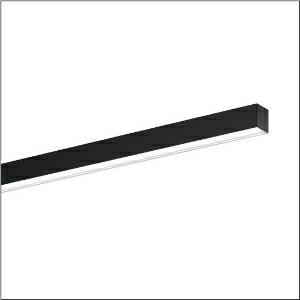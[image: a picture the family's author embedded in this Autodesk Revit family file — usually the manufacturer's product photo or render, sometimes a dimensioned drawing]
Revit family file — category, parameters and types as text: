
# Revit family: silica_21_51mx23tat4b
name_source: partatom
category: Lighting Fixtures
units: mm (PartAtom-declared; Revit-internal decimal feet)

## family parameters
Cut with Voids When Loaded = No
Host = Face
Light Source = No
Part Type = Normal
Room Calculation Point = No
Round Connector Dimension = Use Diameter
Shared = No

## types (1)
- --- (1 x LED, 3230 lm, 32.4 W, 6500K)
    Apparent Load = 32 VA
    CIE Flux Codes = 78 96 99 100 100
    Color Rendering = 80
    Color Temperature = 6500K
    Default Elevation = 1800 mm
    Description = Silica 21, office luminaire, primary optical cover: prismatic diffuser, of PMMA, CAT 2 (L<= 3000cd/m²), light emission: direct distribution, primary light characteristic: symmetric, installation type: surface-mounted, LED, rated luminous flux: 3.230lm, luminous efficacy: 95lm/W, light colour: 8tw, colour temperature: 2700..6500K, control gear: DALI DT8, with terminal, 3+2-pole, max. 2.5mm², mains connection: 220..240V, AC, 50/60Hz, rated input power: 34W, luminaire housing, of aluminium, matt jet black (RAL 9005), length: 1.204mm, width: 53mm, height: 53mm, protection rating (complete): IP20, insulation class (complete): insulation class I (protective earthing), certification: CE, permissible operating ambient temperature: 0..+35°C, standard: EN 50419, packaging unit: 1 piece
    Height = 53 mm
    Lamp = 1 x LED
    Lamp Light Flux = 3230 lm
    Lamp Power = 32.4 W
    Lamp count = 1
    Length = 1204 mm
    Luminous efficacy = 100 lm/W
    Manufacturer = Siteco
    ModVariant = No
    Model = 51MX23TAT4B
    Mounting Place = Ceiling
    Mounting Type = Surface mounted
    Number of Poles = 1
    OnlyDefault = Yes
    Power Factor = 1
    Product Name = Silica 21
    Product group = office luminaire | ceiling mounted
    ProductGroupID = 301
    Protection Class = Protection class I
    Protection Degree = IP 20
    RLX_Detail_Level = 1
    RLX_Emergency_Light_Flux = 0 lm
    RLX_Emergency_Type = 0
    RLX_Emergency_Type_DB = No
    RlxData = <blob elided: 20461 chars, md5=00b5731a>
    Socket = socket
    Standby Power = 0 W
    System Light Flux = 3230 lm
    System Power = 32 W
    Type Comments = individual setting
    Type Image = l_1335925.jpg
    URL = http://relux.com
    VarID = @adj_139313
    Voltage = 0 V
    Weight = 0.00 kg
    Width = 53 mm

## geometry (parser evidence)
native form markers: Blend x4, Sweep x11
no freeform markers — native parametric forms only
